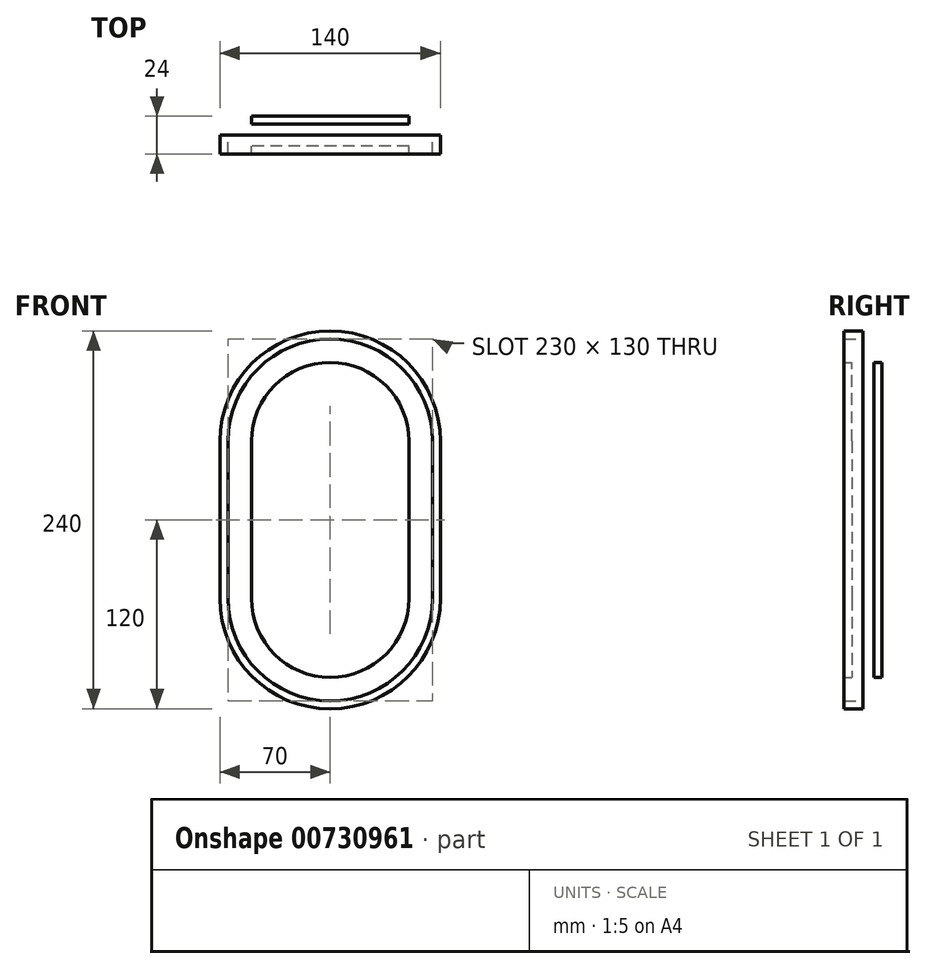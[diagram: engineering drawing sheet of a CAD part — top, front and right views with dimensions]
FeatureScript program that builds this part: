
annotation { "Feature Type Name" : "Feature", "Feature Type Description" : "" }
export const myFeature = defineFeature(function(context is Context, id is Id, definition is map)
    precondition{}
    {
        {
            var Q0;
            Q0=qCreatedBy(makeId("Front.planeOp"),FACE);
            var sketch = newSketch(context, id + "F0", { "sketchPlane" : qUnion([Q0])});
            skLineSegment(sketch, "E0", {"start": v(0, 230) * mm, "end": v(0, 130) * mm, "construction": true});
            skArc(sketch, "E1.0.startCap", {"start": v(-50, 230) * mm, "mid": v(0, 280) * mm, "end": v(50, 230) * mm});
            skArc(sketch, "E1.0.endCap", {"start": v(50, 130) * mm, "mid": v(0, 80) * mm, "end": v(-50, 130) * mm});
            skLineSegment(sketch, "E1.0.left", {"start": v(50, 230) * mm, "end": v(50, 130) * mm});
            skLineSegment(sketch, "E1.0.right", {"start": v(-50, 230) * mm, "end": v(-50, 130) * mm});
            skLineSegment(sketch, "E2.0", {"start": v(70, 230) * mm, "end": v(70, 130) * mm});
            skArc(sketch, "E2.1", {"start": v(-70, 230) * mm, "mid": v(0, 300) * mm, "end": v(70, 230) * mm});
            skLineSegment(sketch, "E2.2", {"start": v(-70, 230) * mm, "end": v(-70, 130) * mm});
            skArc(sketch, "E2.3", {"start": v(70, 130) * mm, "mid": v(0, 60) * mm, "end": v(-70, 130) * mm});
            skLineSegment(sketch, "E3.0", {"start": v(-65, 230) * mm, "end": v(-65, 130) * mm});
            skArc(sketch, "E3.1", {"start": v(-65, 230) * mm, "mid": v(0, 295) * mm, "end": v(65, 230) * mm});
            skLineSegment(sketch, "E3.2", {"start": v(65, 230) * mm, "end": v(65, 130) * mm});
            skArc(sketch, "E3.3", {"start": v(65, 130) * mm, "mid": v(0, 65) * mm, "end": v(-65, 130) * mm});
            skSolve(sketch);
        }
        {
            var Q0;
            Q0=makeQuery(id+"F0.imprint","IMPRINT",FACE,{"disambiguationData":[TD([[makeQuery(id+"F0.imprint","IMPRINT",EDGE,{"derivedFrom":sQuery(id+"F0.wireOp",EDGE,"E1.0.startCap")}),1.0]])]});
            var Q1;
            Q1=makeQuery(id+"F0.imprint","IMPRINT",FACE,{"disambiguationData":[TD([[makeQuery(id+"F0.imprint","IMPRINT",EDGE,{"derivedFrom":sQuery(id+"F0.wireOp",EDGE,"E2.0")}),-1.0]])]});
            extrude(context, id + "F1", {"entities" : qUnion([Q0, Q1]), "depth" : 12 * mm, "offsetDistance" : 25 * mm});
        }
        {
            var Q0;
            Q0=makeQuery(id+"F0.imprint","IMPRINT",FACE,{"disambiguationData":[TD([[makeQuery(id+"F0.imprint","IMPRINT",EDGE,{"derivedFrom":sQuery(id+"F0.wireOp",EDGE,"E1.0.startCap")}),1.0]])]});
            extrude(context, id + "F2", {"entities" : qUnion([Q0]), "operationType" : NewBodyOperationType.REMOVE, "depth" : 7 * mm, "offsetDistance" : 25 * mm});
        }
        {
            var Q0;
            Q0=makeQuery(id+"F1.opExtrude","SWEPT_BODY",BODY,{"disambiguationData":[OSD([sQuery(id+"F0.wireOp",EDGE,"E1.0.startCap"),sQuery(id+"F0.wireOp",EDGE,"E1.0.endCap"),sQuery(id+"F0.wireOp",EDGE,"E1.0.left"),sQuery(id+"F0.wireOp",EDGE,"E1.0.right"),sQuery(id+"F0.wireOp",EDGE,"E2.0"),sQuery(id+"F0.wireOp",EDGE,"E2.1"),sQuery(id+"F0.wireOp",EDGE,"E2.2"),sQuery(id+"F0.wireOp",EDGE,"E2.3")])]});
            var Q1;
            Q1=qCreatedBy(makeId("Front.planeOp"),FACE);
            mirror(context, id + "F3", {"operationType" : NewBodyOperationType.ADD, "entities" : qUnion([Q0]), "mirrorPlane" : qUnion([Q1])});
        }
    });
